# Revit family: EURS_63_LF_FB_WL140V
name_source: partatom
category: Lighting Fixtures
units: mm (PartAtom-declared; Revit-internal decimal feet)

## family parameters
Cut with Voids When Loaded = No
Host = Face
Light Source = No
Part Type = Normal
Room Calculation Point = No
Round Connector Dimension = Use Diameter
Shared = Yes

## types (1)
- Type catalog
    Apparent Load = 0 VA
    BIM Library - URL = http://www.lighting.philips.com
    Content modified date = 05-01-2022
    Content version = 1.0
    Default Elevation = 0 mm  [stored 0 ft]
    ETIM code = MODEL ETIM CODE
    ETIM code URL = ETIM CODE WEBPAGE
    Height = 85 mm  [stored 0.278871 ft]
    Lamp = LAMP TYPE
    Lamp type = WL140V IES Data : PSU 1 xLED12S_830 O
    Last IES update = 05-01-2022
    Length = 390 mm  [stored 1.27953 ft]
    Light source = 2 mm  [stored 0.00656168 ft]
    Manufacturer = Philips
    Order code = ORDER CODE
    Product catalog - URL = MODEL WEBPAGE
    Rim height = 5 mm  [stored 0.0164042 ft]
    Type Comments = Face Based
    URL = http://www.lighting.philips.com
    Voltage (V) = 230 V
    Width = 390 mm  [stored 1.27953 ft]

note: [stored X ft] marks values corroborated as IEEE doubles in the binary element streams (Revit-internal decimal feet)

## geometry (parser evidence)
native form markers: Sweep x14
no freeform markers — native parametric forms only
